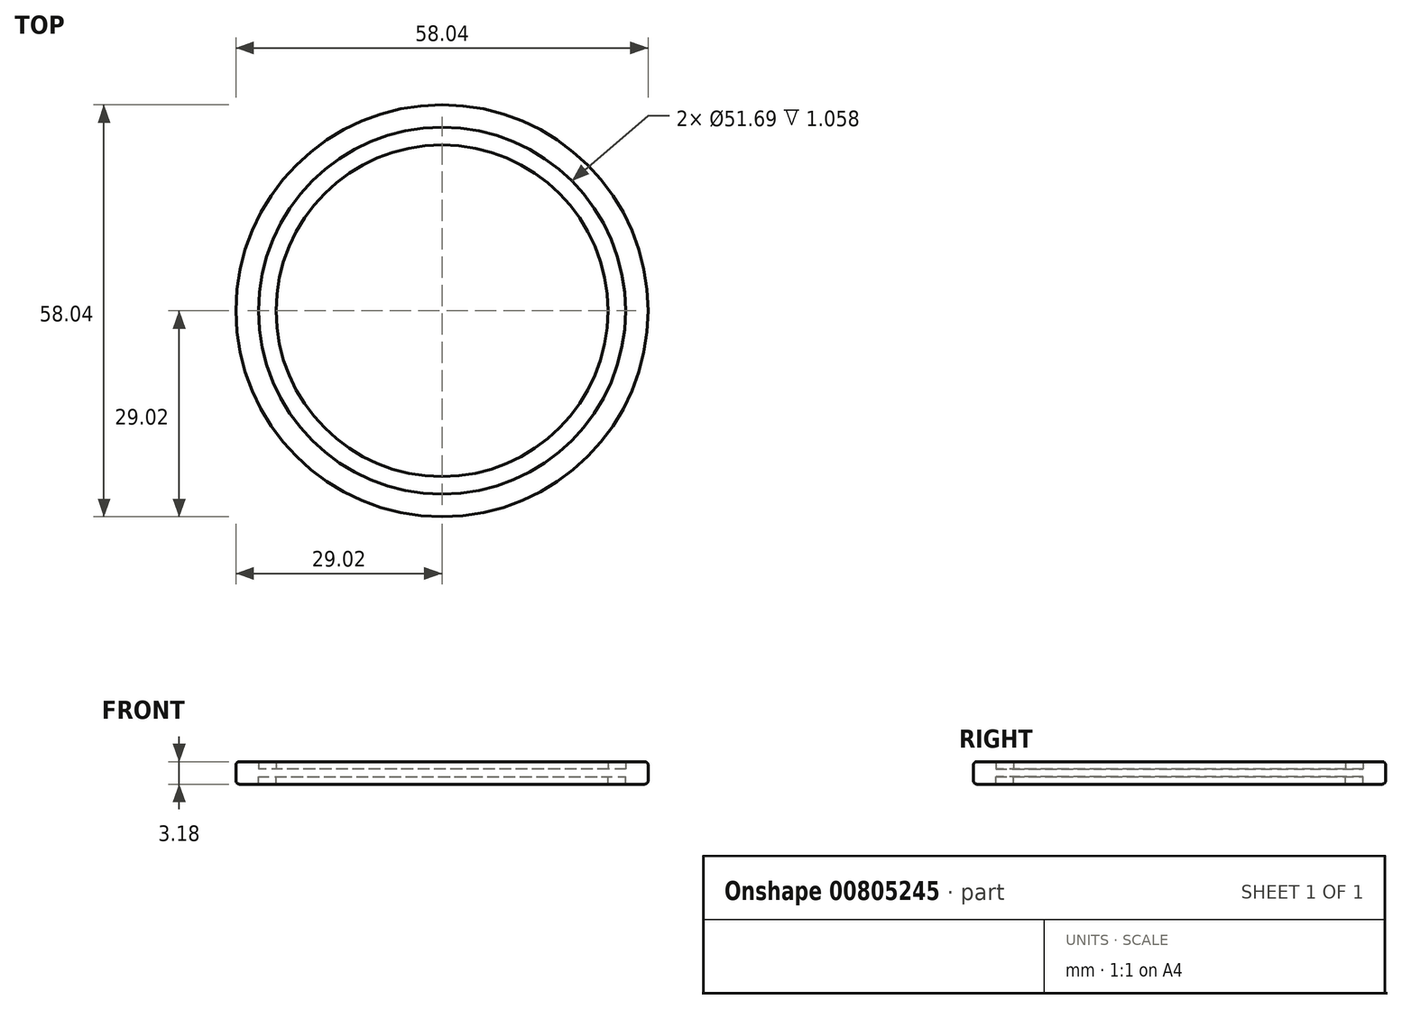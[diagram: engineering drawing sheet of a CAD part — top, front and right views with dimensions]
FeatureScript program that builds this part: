
annotation { "Feature Type Name" : "Feature", "Feature Type Description" : "" }
export const myFeature = defineFeature(function(context is Context, id is Id, definition is map)
    precondition{}
    {
        {
            var Q0;
            Q0=qCreatedBy(makeId("Top.planeOp"),FACE);
            var sketch = newSketch(context, id + "F0", { "sketchPlane" : qUnion([Q0])});
            skCircle(sketch, "E0", {"center": v(0, 0) * mm, "radius": 25.84 * mm});
            skCircle(sketch, "E1", {"center": v(0, 0) * mm, "radius": 23.37 * mm});
            skPoint(sketch, "E2.visualSharp", {"position": v(32.39, -8.32) * mm});
            skPoint(sketch, "E3.visualSharp", {"position": v(22.95, -24.67) * mm});
            skPoint(sketch, "E4.visualSharp", {"position": v(8.97, 32.2) * mm});
            skPoint(sketch, "E5.visualSharp", {"position": v(-9.91, 32.2) * mm});
            skPoint(sketch, "E6.visualSharp", {"position": v(-32.7, -7.8) * mm});
            skPoint(sketch, "E7.visualSharp", {"position": v(-23.25, -24.14) * mm});
            skPoint(sketch, "E8.visualSharp", {"position": v(-8.16, 27.85) * mm});
            skPoint(sketch, "E9.visualSharp", {"position": v(7.38, 28.07) * mm});
            skPoint(sketch, "E10.visualSharp", {"position": v(28, -7.63) * mm});
            skPoint(sketch, "E11.visualSharp", {"position": v(20.05, -20.98) * mm});
            skPoint(sketch, "E12.visualSharp", {"position": v(-20.42, -20.61) * mm});
            skPoint(sketch, "E13.visualSharp", {"position": v(-28.13, -7.12) * mm});
            skCircle(sketch, "E14", {"center": v(0, 0) * mm, "radius": 29.02 * mm});
            skSolve(sketch);
        }
        {
            var Q0;
            Q0=makeQuery(id+"F0.imprint","IMPRINT",FACE,{"disambiguationData":[TD([[makeQuery(id+"F0.imprint","IMPRINT",EDGE,{"derivedFrom":sQuery(id+"F0.wireOp",EDGE,"E1")}),1.0]])]});
            var Q1;
            Q1=makeQuery(id+"F0.imprint","IMPRINT",FACE,{"disambiguationData":[TD([[makeQuery(id+"F0.imprint","IMPRINT",EDGE,{"derivedFrom":sQuery(id+"F0.wireOp",EDGE,"E0")}),-1.0]])]});
            extrude(context, id + "F1", {"entities" : qUnion([Q0, Q1]), "depth" : 1.06 * mm, "offsetDistance" : 25.4 * mm});
        }
        {
            var Q0;
            Q0=makeQuery(id+"F1.opExtrude","CAP_FACE",FACE,{"disambiguationData":[OSD([sQuery(id+"F0.wireOp",EDGE,"E1")])],"isStart":true});
            var sketch = newSketch(context, id + "F2", { "sketchPlane" : qUnion([Q0])});
            skCircle(sketch, "E15.0", {"center": v(0, 0) * mm, "radius": 29.02 * mm});
            skSolve(sketch);
        }
        {
            var Q0;
            Q0=makeQuery(id+"F2.imprint","IMPRINT",FACE,{"disambiguationData":[TD([[makeQuery(id+"F2.imprint","IMPRINT",EDGE,{"derivedFrom":makeQuery(id+"F1.opExtrude","CAP_EDGE",EDGE,{"disambiguationData":[OSD([sQuery(id+"F0.wireOp",EDGE,"E1")])],"isStart":true})}),-1.0]])]});
            var Q1;
            Q1=makeQuery(id+"F2.imprint","IMPRINT",FACE,{"disambiguationData":[TD([[makeQuery(id+"F2.imprint","IMPRINT",EDGE,{"derivedFrom":sQuery(id+"F2.wireOp",EDGE,"E15.0")}),1.0]])]});
            extrude(context, id + "F3", {"entities" : qUnion([Q0, Q1]), "operationType" : NewBodyOperationType.ADD, "depth" : 1.06 * mm, "offsetDistance" : 25.4 * mm});
        }
        {
            var Q0;
            Q0=makeQuery(id+"F3.opExtrude","CAP_FACE",FACE,{"disambiguationData":[OSD([sQuery(id+"F2.wireOp",EDGE,"E15.0")])],"isStart":false});
            var sketch = newSketch(context, id + "F4", { "sketchPlane" : qUnion([Q0])});
            skCircle(sketch, "E16.0", {"center": v(0, 0) * mm, "radius": 23.37 * mm});
            skCircle(sketch, "E17.0", {"center": v(0, 0) * mm, "radius": 25.84 * mm});
            skCircle(sketch, "E18.0", {"center": v(0, 0) * mm, "radius": 29.02 * mm});
            skSolve(sketch);
        }
        {
            var Q0;
            Q0=makeQuery(id+"F4.imprint","IMPRINT",FACE,{"disambiguationData":[TD([[makeQuery(id+"F4.imprint","IMPRINT",EDGE,{"derivedFrom":sQuery(id+"F4.wireOp",EDGE,"E16.0")}),1.0]])]});
            var Q1;
            Q1=makeQuery(id+"F4.imprint","IMPRINT",FACE,{"disambiguationData":[TD([[makeQuery(id+"F4.imprint","IMPRINT",EDGE,{"derivedFrom":sQuery(id+"F4.wireOp",EDGE,"E17.0")}),-1.0]])]});
            extrude(context, id + "F5", {"entities" : qUnion([Q0, Q1]), "operationType" : NewBodyOperationType.ADD, "depth" : 1.06 * mm, "offsetDistance" : 25.4 * mm});
        }
        {
            var Q0;
            Q0=makeQuery(id+"F5.opExtrude","CAP_EDGE",EDGE,{"disambiguationData":[OSD([sQuery(id+"F4.wireOp",EDGE,"E18.0")])],"isStart":false});
            var Q1;
            Q1=makeQuery(id+"F1.opExtrude","CAP_EDGE",EDGE,{"disambiguationData":[OSD([sQuery(id+"F0.wireOp",EDGE,"E14")])],"isStart":false});
            fillet(context, id + "F6", {"entities" : qUnion([Q0, Q1]), "radius" : 0.5 * mm, "tangentPropagation" : true, "allowEdgeOverflow" : false});
        }
    });
